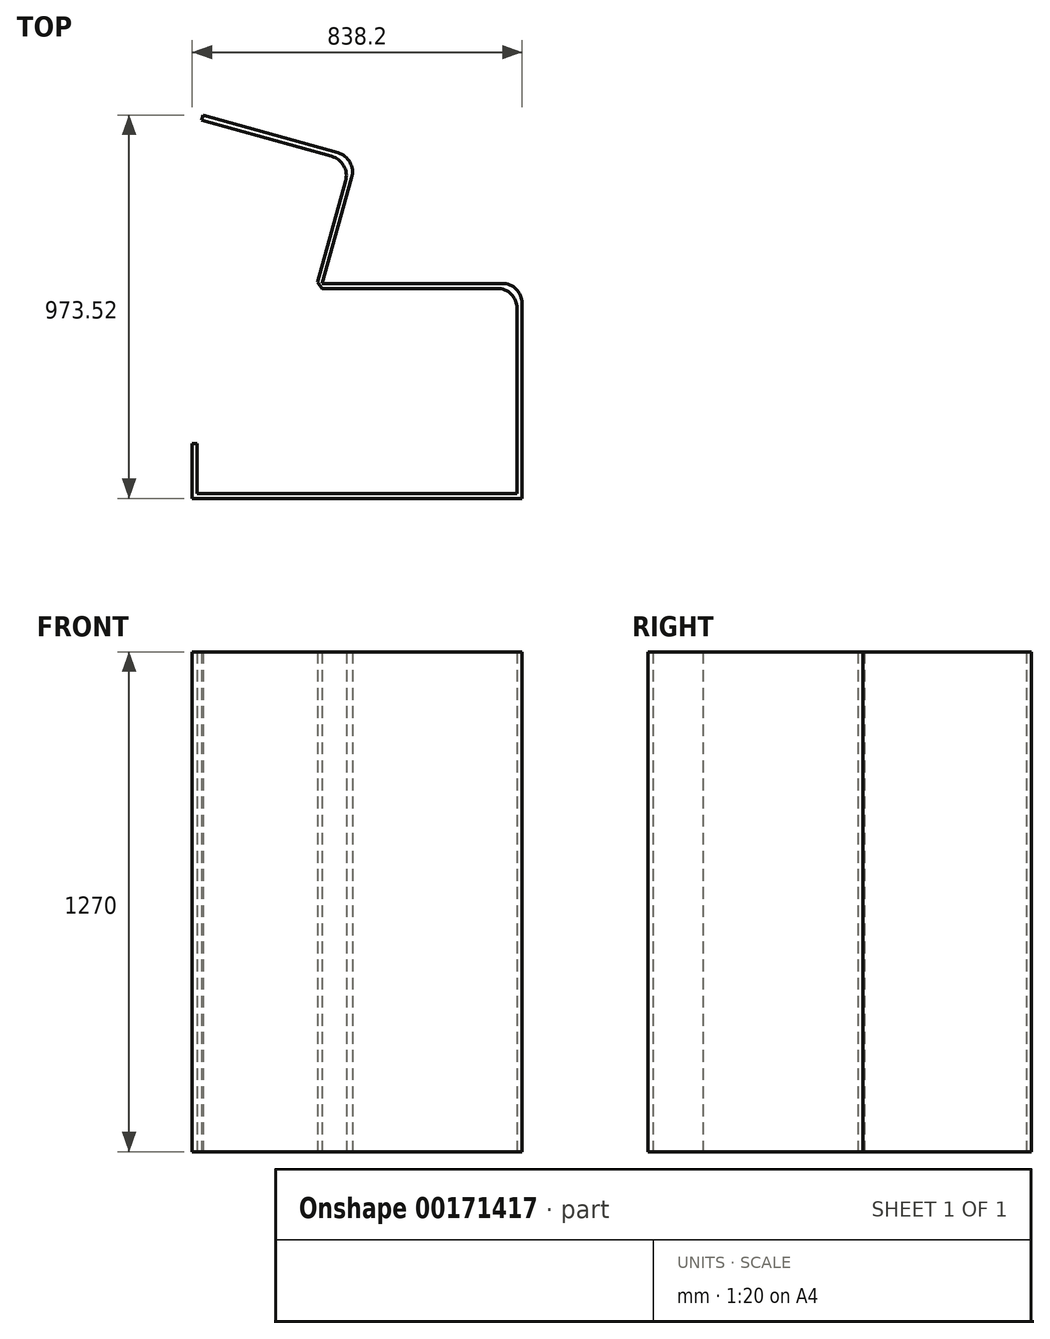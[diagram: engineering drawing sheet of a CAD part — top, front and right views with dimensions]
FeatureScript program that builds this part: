
annotation { "Feature Type Name" : "Feature", "Feature Type Description" : "" }
export const myFeature = defineFeature(function(context is Context, id is Id, definition is map)
    precondition{}
    {
        {
            var Q0;
            Q0=qCreatedBy(makeId("Top.planeOp"),FACE);
            var sketch = newSketch(context, id + "F0", { "sketchPlane" : qUnion([Q0])});
            skLineSegment(sketch, "E0.bottom", {"start": v(-419.1, 6.35) * mm, "end": v(419.1, 6.35) * mm});
            skLineSegment(sketch, "E0.top", {"start": v(-419.1, -6.35) * mm, "end": v(419.1, -6.35) * mm});
            skLineSegment(sketch, "E0.left", {"start": v(-419.1, 6.35) * mm, "end": v(-419.1, -6.35) * mm});
            skLineSegment(sketch, "E0.right", {"start": v(419.1, 6.35) * mm, "end": v(419.1, -6.35) * mm});
            skPoint(sketch, "E0.middle", {"position": v(0, 0) * mm});
            skLineSegment(sketch, "E1", {"start": v(419.1, 6.35) * mm, "end": v(419.1, 488.95) * mm});
            skLineSegment(sketch, "E2", {"start": v(368.3, 539.75) * mm, "end": v(-88.9, 539.75) * mm});
            skLineSegment(sketch, "E3", {"start": v(-419.1, 6.35) * mm, "end": v(-419.1, 133.35) * mm});
            skLineSegment(sketch, "E4", {"start": v(-88.9, 539.75) * mm, "end": v(-13.68, 808.83) * mm});
            skLineSegment(sketch, "E5", {"start": v(-48.92, 871.43) * mm, "end": v(-391.4, 967.17) * mm});
            skLineSegment(sketch, "E6", {"start": v(-419.1, 133.35) * mm, "end": v(-406.4, 133.35) * mm});
            skLineSegment(sketch, "E7", {"start": v(406.4, 6.35) * mm, "end": v(406.4, 476.25) * mm});
            skLineSegment(sketch, "E8", {"start": v(355.6, 527.05) * mm, "end": v(-88.9, 527.05) * mm});
            skLineSegment(sketch, "E9", {"start": v(-406.4, 133.35) * mm, "end": v(-406.4, 6.35) * mm});
            skPoint(sketch, "E10.visualSharp", {"position": v(419.1, 539.75) * mm});
            skArc(sketch, "E10.filletArc", {"start": v(419.1, 488.95) * mm, "mid": v(404.22, 524.87) * mm, "end": v(368.3, 539.75) * mm});
            skPoint(sketch, "E11.visualSharp", {"position": v(406.4, 527.05) * mm});
            skArc(sketch, "E11.filletArc", {"start": v(406.4, 476.25) * mm, "mid": v(391.52, 512.17) * mm, "end": v(355.6, 527.05) * mm});
            skLineSegment(sketch, "E12", {"start": v(-88.9, 539.75) * mm, "end": v(-88.9, 527.05) * mm, "construction": true});
            skLineSegment(sketch, "E13", {"start": v(-391.4, 967.17) * mm, "end": v(-394.81, 954.94) * mm});
            skLineSegment(sketch, "E14", {"start": v(-394.81, 954.94) * mm, "end": v(-64.57, 862.62) * mm});
            skLineSegment(sketch, "E15", {"start": v(-88.9, 539.75) * mm, "end": v(-101.13, 543.17) * mm, "construction": true});
            skLineSegment(sketch, "E16", {"start": v(-29.33, 800.02) * mm, "end": v(-101.13, 543.17) * mm});
            skPoint(sketch, "E17.visualSharp", {"position": v(0, 857.76) * mm});
            skArc(sketch, "E17.filletArc", {"start": v(-13.68, 808.83) * mm, "mid": v(-18.34, 847.43) * mm, "end": v(-48.92, 871.43) * mm});
            skPoint(sketch, "E18.visualSharp", {"position": v(-15.65, 848.95) * mm});
            skArc(sketch, "E18.filletArc", {"start": v(-29.33, 800.02) * mm, "mid": v(-33.99, 838.62) * mm, "end": v(-64.57, 862.62) * mm});
            skLineSegment(sketch, "E19", {"start": v(-101.13, 543.17) * mm, "end": v(-88.9, 527.05) * mm});
            skSolve(sketch);
        }
        {
            var Q0;
            Q0 = qSketchRegion(id + "F0", true);
            extrude(context, id + "F1", {"entities" : qUnion([Q0]), "depth" : 1270 * mm});
        }
    });
